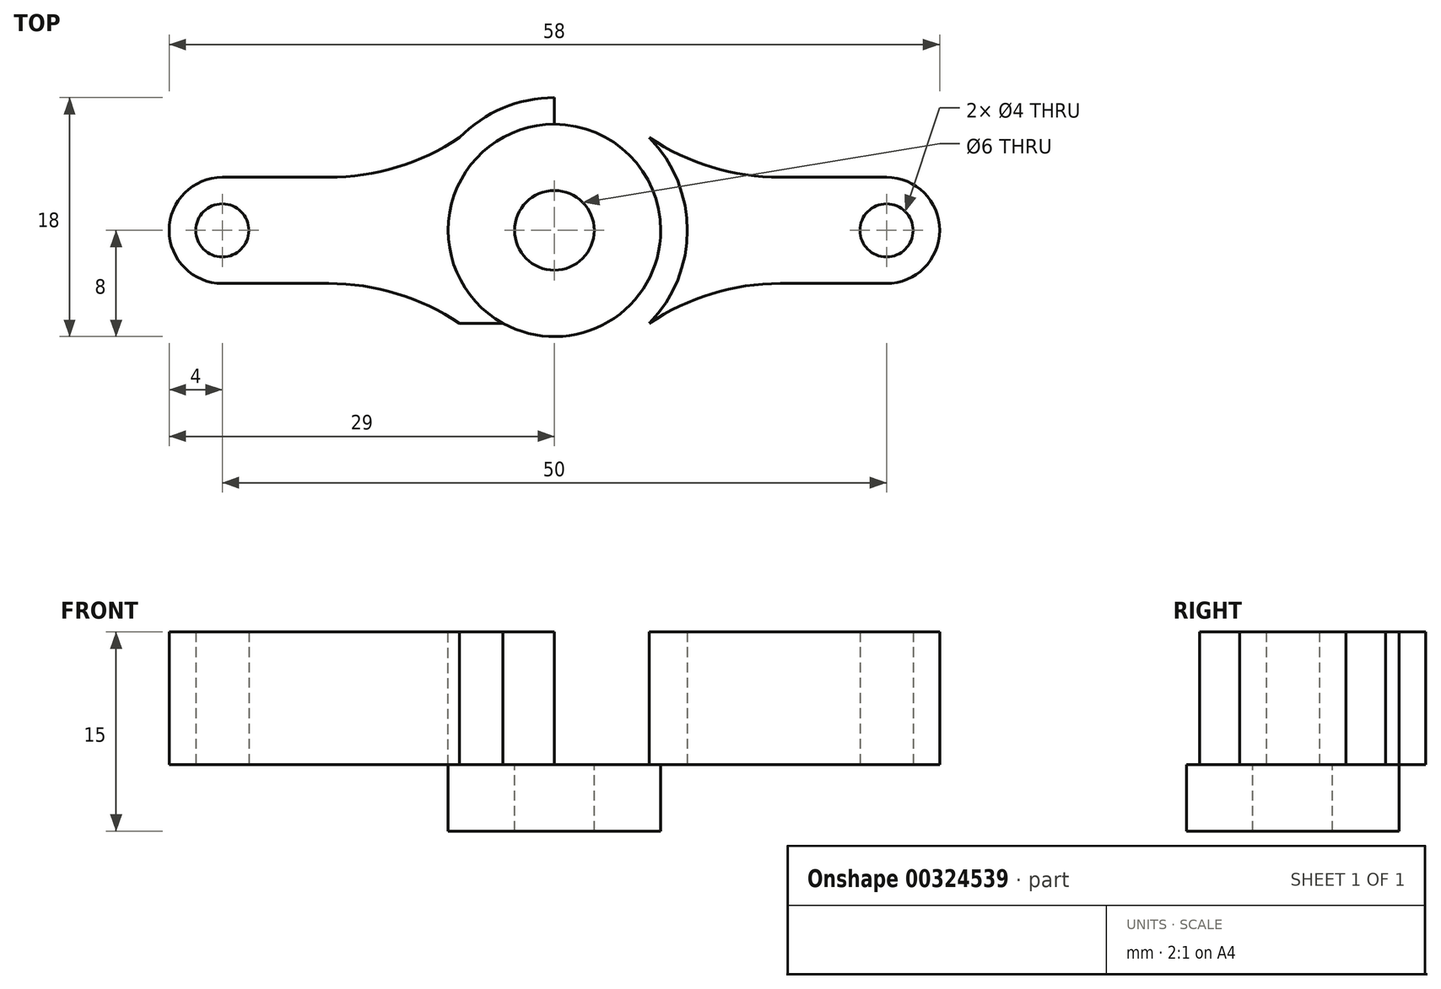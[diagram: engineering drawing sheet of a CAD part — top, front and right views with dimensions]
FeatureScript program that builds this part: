
annotation { "Feature Type Name" : "Feature", "Feature Type Description" : "" }
export const myFeature = defineFeature(function(context is Context, id is Id, definition is map)
    precondition{}
    {
        {
            var Q0;
            Q0=qCreatedBy(makeId("Top.planeOp"),FACE);
            var sketch = newSketch(context, id + "F0", { "sketchPlane" : qUnion([Q0])});
            skCircle(sketch, "E0", {"center": v(0, 0) * mm, "radius": 10 * mm});
            skCircle(sketch, "E1", {"center": v(25, 0) * mm, "radius": 4 * mm});
            skCircle(sketch, "E2", {"center": v(-25, 0) * mm, "radius": 4 * mm});
            skLineSegment(sketch, "E3", {"start": v(-25, 0) * mm, "end": v(-25, 4) * mm});
            skLineSegment(sketch, "E4", {"start": v(25, 0) * mm, "end": v(25, 4) * mm});
            skLineSegment(sketch, "E5", {"start": v(25, 0) * mm, "end": v(25, -4) * mm});
            skLineSegment(sketch, "E6", {"start": v(-25, 0) * mm, "end": v(-25, -4) * mm});
            skLineSegment(sketch, "E7", {"start": v(0, 0) * mm, "end": v(0, 10) * mm});
            skLineSegment(sketch, "E8", {"start": v(0, 10) * mm, "end": v(0, -10) * mm});
            skLineSegment(sketch, "E9", {"start": v(0, 7) * mm, "end": v(0, 10) * mm});
            skLineSegment(sketch, "E10", {"start": v(0, 7) * mm, "end": v(7.14, 7) * mm});
            skLineSegment(sketch, "E11", {"start": v(7.14, 7) * mm, "end": v(-7.14, 7) * mm});
            skLineSegment(sketch, "E12", {"start": v(25, 4) * mm, "end": v(17, 4) * mm});
            skArc(sketch, "E13", {"start": v(17, 4) * mm, "mid": v(11.85, 4.77) * mm, "end": v(7.14, 7) * mm});
            skLineSegment(sketch, "E14", {"start": v(0, -10) * mm, "end": v(0, -7) * mm});
            skLineSegment(sketch, "E15", {"start": v(0, -7) * mm, "end": v(7.14, -7) * mm});
            skLineSegment(sketch, "E16", {"start": v(7.14, -7) * mm, "end": v(-7.14, -7) * mm});
            skLineSegment(sketch, "E17", {"start": v(25, -4) * mm, "end": v(17, -4) * mm});
            skArc(sketch, "E18", {"start": v(17, -4) * mm, "mid": v(11.85, -4.77) * mm, "end": v(7.14, -7) * mm});
            skLineSegment(sketch, "E19", {"start": v(-25, 4) * mm, "end": v(-17, 4) * mm});
            skLineSegment(sketch, "E20", {"start": v(-25, -4) * mm, "end": v(-17, -4) * mm});
            skArc(sketch, "E21", {"start": v(-17, 4) * mm, "mid": v(-11.85, 4.77) * mm, "end": v(-7.14, 7) * mm});
            skArc(sketch, "E22", {"start": v(-17, -4) * mm, "mid": v(-11.85, -4.77) * mm, "end": v(-7.14, -7) * mm});
            skCircle(sketch, "E23", {"center": v(0, 0) * mm, "radius": 7.5 * mm});
            skCircle(sketch, "E24", {"center": v(0, 0) * mm, "radius": 3 * mm});
            skCircle(sketch, "E25", {"center": v(-25, 0) * mm, "radius": 2 * mm});
            skCircle(sketch, "E26", {"center": v(25, 0) * mm, "radius": 2 * mm});
            skSolve(sketch);
        }
        {
            var Q0;
            {var subQ0=sQuery(id+"F0.wireOp",EDGE,"E3");var subQ5=sQuery(id+"F0.wireOp",EDGE,"E25");var subQ6=makeQuery(id+"F0.imprint","INTERSECT",VERTEX,{"derivedFrom":[subQ0,subQ5]});Q0=makeQuery(id+"F0.imprint","IMPRINT",FACE,{"disambiguationData":[TD([[makeQuery(id+"F0.imprint","IMPRINT",EDGE,{"disambiguationData":[TD([[subQ6,-1.0]])],"derivedFrom":subQ5}),-1.0]])]});}
            var Q1;
            {var subQ0=sQuery(id+"F0.wireOp",EDGE,"E3");var subQ5=sQuery(id+"F0.wireOp",EDGE,"E25");var subQ6=makeQuery(id+"F0.imprint","INTERSECT",VERTEX,{"derivedFrom":[subQ0,subQ5]});Q1=makeQuery(id+"F0.imprint","IMPRINT",FACE,{"disambiguationData":[TD([[makeQuery(id+"F0.imprint","IMPRINT",EDGE,{"disambiguationData":[TD([[subQ6,1.0]])],"derivedFrom":subQ5}),-1.0]])]});}
            var Q2;
            {var subQ0=sQuery(id+"F0.wireOp",EDGE,"E19");Q2=makeQuery(id+"F0.imprint","IMPRINT",FACE,{"disambiguationData":[TD([[makeQuery(id+"F0.imprint","IMPRINT",EDGE,{"derivedFrom":subQ0}),-1.0]])]});}
            var Q3;
            {var subQ0=sQuery(id+"F0.wireOp",EDGE,"E11");var subQ5=sQuery(id+"F0.wireOp",EDGE,"E23");var subQ6=makeQuery(id+"F0.imprint","INTERSECT",VERTEX,{"disambiguationData":[OD(1.0)],"derivedFrom":[subQ0,subQ5]});Q3=makeQuery(id+"F0.imprint","IMPRINT",FACE,{"disambiguationData":[TD([[makeQuery(id+"F0.imprint","IMPRINT",EDGE,{"disambiguationData":[TD([[subQ6,-1.0]])],"derivedFrom":subQ5}),-1.0]])]});}
            var Q4;
            {var subQ0=sQuery(id+"F0.wireOp",EDGE,"E11");var subQ5=sQuery(id+"F0.wireOp",EDGE,"E23");var subQ6=makeQuery(id+"F0.imprint","INTERSECT",VERTEX,{"disambiguationData":[OD(0.0)],"derivedFrom":[subQ0,subQ5]});Q4=makeQuery(id+"F0.imprint","IMPRINT",FACE,{"disambiguationData":[TD([[makeQuery(id+"F0.imprint","IMPRINT",EDGE,{"disambiguationData":[TD([[subQ6,1.0]])],"derivedFrom":subQ5}),-1.0]])]});}
            var Q5;
            {var subQ0=sQuery(id+"F0.wireOp",EDGE,"E8");var subQ1=makeQuery(id+"F0.imprint","IMPRINT",VERTEX,{"derivedFrom":subQ0});Q5=makeQuery(id+"F0.imprint","IMPRINT",FACE,{"disambiguationData":[TD([[makeQuery(id+"F0.imprint","IMPRINT",EDGE,{"disambiguationData":[TD([[subQ1,1.0]])],"derivedFrom":subQ0}),1.0]])]});}
            var Q6;
            {var subQ0=sQuery(id+"F0.wireOp",EDGE,"E8");var subQ1=makeQuery(id+"F0.imprint","IMPRINT",VERTEX,{"derivedFrom":subQ0});Q6=makeQuery(id+"F0.imprint","IMPRINT",FACE,{"disambiguationData":[TD([[makeQuery(id+"F0.imprint","IMPRINT",EDGE,{"disambiguationData":[TD([[subQ1,1.0]])],"derivedFrom":subQ0}),-1.0]])]});}
            var Q7;
            {var subQ1=sQuery(id+"F0.wireOp",EDGE,"E12");Q7=makeQuery(id+"F0.imprint","IMPRINT",FACE,{"disambiguationData":[TD([[makeQuery(id+"F0.imprint","IMPRINT",EDGE,{"derivedFrom":subQ1}),1.0]])]});}
            var Q8;
            {var subQ1=sQuery(id+"F0.wireOp",EDGE,"E14");var subQ3=sQuery(id+"F0.wireOp",EDGE,"E23");var subQ4=makeQuery(id+"F0.imprint","INTERSECT",VERTEX,{"derivedFrom":[subQ1,subQ3]});Q8=makeQuery(id+"F0.imprint","IMPRINT",FACE,{"disambiguationData":[TD([[makeQuery(id+"F0.imprint","IMPRINT",EDGE,{"disambiguationData":[TD([[subQ4,1.0]])],"derivedFrom":subQ3}),1.0]])]});}
            var Q9;
            {var subQ1=sQuery(id+"F0.wireOp",EDGE,"E14");var subQ3=sQuery(id+"F0.wireOp",EDGE,"E23");var subQ4=makeQuery(id+"F0.imprint","INTERSECT",VERTEX,{"derivedFrom":[subQ1,subQ3]});Q9=makeQuery(id+"F0.imprint","IMPRINT",FACE,{"disambiguationData":[TD([[makeQuery(id+"F0.imprint","IMPRINT",EDGE,{"disambiguationData":[TD([[subQ4,-1.0]])],"derivedFrom":subQ3}),1.0]])]});}
            var Q10;
            {var subQ0=sQuery(id+"F0.wireOp",EDGE,"E14");var subQ1=sQuery(id+"F0.wireOp",EDGE,"E0");var subQ2=makeQuery(id+"F0.imprint","INTERSECT",VERTEX,{"derivedFrom":[subQ1,subQ0]});Q10=makeQuery(id+"F0.imprint","IMPRINT",FACE,{"disambiguationData":[TD([[makeQuery(id+"F0.imprint","IMPRINT",EDGE,{"disambiguationData":[TD([[subQ2,-1.0]])],"derivedFrom":subQ0}),-1.0]])]});}
            var Q11;
            {var subQ0=sQuery(id+"F0.wireOp",EDGE,"E14");var subQ1=sQuery(id+"F0.wireOp",EDGE,"E0");var subQ2=makeQuery(id+"F0.imprint","INTERSECT",VERTEX,{"derivedFrom":[subQ1,subQ0]});Q11=makeQuery(id+"F0.imprint","IMPRINT",FACE,{"disambiguationData":[TD([[makeQuery(id+"F0.imprint","IMPRINT",EDGE,{"disambiguationData":[TD([[subQ2,-1.0]])],"derivedFrom":subQ0}),1.0]])]});}
            var Q12;
            {var subQ3=sQuery(id+"F0.wireOp",EDGE,"E23");var subQ5=sQuery(id+"F0.wireOp",EDGE,"E11");var subQ7=makeQuery(id+"F0.imprint","INTERSECT",VERTEX,{"disambiguationData":[OD(1.0)],"derivedFrom":[subQ5,subQ3]});Q12=makeQuery(id+"F0.imprint","IMPRINT",FACE,{"disambiguationData":[TD([[makeQuery(id+"F0.imprint","IMPRINT",EDGE,{"disambiguationData":[TD([[subQ7,-1.0]])],"derivedFrom":subQ3}),1.0]])]});}
            var Q13;
            {var subQ0=sQuery(id+"F0.wireOp",EDGE,"E11");var subQ3=sQuery(id+"F0.wireOp",EDGE,"E23");var subQ4=makeQuery(id+"F0.imprint","INTERSECT",VERTEX,{"disambiguationData":[OD(0.0)],"derivedFrom":[subQ0,subQ3]});Q13=makeQuery(id+"F0.imprint","IMPRINT",FACE,{"disambiguationData":[TD([[makeQuery(id+"F0.imprint","IMPRINT",EDGE,{"disambiguationData":[TD([[subQ4,1.0]])],"derivedFrom":subQ3}),1.0]])]});}
            var Q14;
            {var subQ0=sQuery(id+"F0.wireOp",EDGE,"E4");var subQ5=sQuery(id+"F0.wireOp",EDGE,"E26");var subQ6=makeQuery(id+"F0.imprint","INTERSECT",VERTEX,{"derivedFrom":[subQ0,subQ5]});Q14=makeQuery(id+"F0.imprint","IMPRINT",FACE,{"disambiguationData":[TD([[makeQuery(id+"F0.imprint","IMPRINT",EDGE,{"disambiguationData":[TD([[subQ6,-1.0]])],"derivedFrom":subQ5}),-1.0]])]});}
            var Q15;
            {var subQ0=sQuery(id+"F0.wireOp",EDGE,"E4");var subQ5=sQuery(id+"F0.wireOp",EDGE,"E26");var subQ6=makeQuery(id+"F0.imprint","INTERSECT",VERTEX,{"derivedFrom":[subQ0,subQ5]});Q15=makeQuery(id+"F0.imprint","IMPRINT",FACE,{"disambiguationData":[TD([[makeQuery(id+"F0.imprint","IMPRINT",EDGE,{"disambiguationData":[TD([[subQ6,1.0]])],"derivedFrom":subQ5}),-1.0]])]});}
            var Q16;
            {var subQ1=sQuery(id+"F0.wireOp",EDGE,"E9");var subQ3=sQuery(id+"F0.wireOp",EDGE,"E23");var subQ4=makeQuery(id+"F0.imprint","INTERSECT",VERTEX,{"derivedFrom":[subQ1,subQ3]});Q16=makeQuery(id+"F0.imprint","IMPRINT",FACE,{"disambiguationData":[TD([[makeQuery(id+"F0.imprint","IMPRINT",EDGE,{"disambiguationData":[TD([[subQ4,-1.0]])],"derivedFrom":subQ3}),1.0]])]});}
            var Q17;
            {var subQ1=sQuery(id+"F0.wireOp",EDGE,"E9");var subQ3=sQuery(id+"F0.wireOp",EDGE,"E23");var subQ4=makeQuery(id+"F0.imprint","INTERSECT",VERTEX,{"derivedFrom":[subQ1,subQ3]});Q17=makeQuery(id+"F0.imprint","IMPRINT",FACE,{"disambiguationData":[TD([[makeQuery(id+"F0.imprint","IMPRINT",EDGE,{"disambiguationData":[TD([[subQ4,1.0]])],"derivedFrom":subQ3}),1.0]])]});}
            var Q18;
            {var subQ0=sQuery(id+"F0.wireOp",EDGE,"E9");var subQ1=sQuery(id+"F0.wireOp",EDGE,"E0");var subQ2=makeQuery(id+"F0.imprint","INTERSECT",VERTEX,{"derivedFrom":[subQ1,subQ0]});Q18=makeQuery(id+"F0.imprint","IMPRINT",FACE,{"disambiguationData":[TD([[makeQuery(id+"F0.imprint","IMPRINT",EDGE,{"disambiguationData":[TD([[subQ2,1.0]])],"derivedFrom":subQ0}),1.0]])]});}
            var Q19;
            {var subQ0=sQuery(id+"F0.wireOp",EDGE,"E9");var subQ1=sQuery(id+"F0.wireOp",EDGE,"E0");var subQ2=makeQuery(id+"F0.imprint","INTERSECT",VERTEX,{"derivedFrom":[subQ1,subQ0]});Q19=makeQuery(id+"F0.imprint","IMPRINT",FACE,{"disambiguationData":[TD([[makeQuery(id+"F0.imprint","IMPRINT",EDGE,{"disambiguationData":[TD([[subQ2,1.0]])],"derivedFrom":subQ0}),-1.0]])]});}
            extrude(context, id + "F1", {"entities" : qUnion([Q0, Q1, Q2, Q3, Q4, Q5, Q6, Q7, Q8, Q9, Q10, Q11, Q12, Q13, Q14, Q15, Q16, Q17, Q18, Q19]), "depth" : 10 * mm});
        }
        {
            var Q0;
            Q0=makeQuery(id+"F1.opExtrude","CAP_FACE",FACE,{"disambiguationData":[OSD([sQuery(id+"F0.wireOp",EDGE,"E0"),sQuery(id+"F0.wireOp",EDGE,"E1"),sQuery(id+"F0.wireOp",EDGE,"E2"),sQuery(id+"F0.wireOp",EDGE,"E12"),sQuery(id+"F0.wireOp",EDGE,"E13"),sQuery(id+"F0.wireOp",EDGE,"E17"),sQuery(id+"F0.wireOp",EDGE,"E18"),sQuery(id+"F0.wireOp",EDGE,"E19"),sQuery(id+"F0.wireOp",EDGE,"E20"),sQuery(id+"F0.wireOp",EDGE,"E21"),sQuery(id+"F0.wireOp",EDGE,"E22"),sQuery(id+"F0.wireOp",EDGE,"E25"),sQuery(id+"F0.wireOp",EDGE,"E26")])],"isStart":false});
            var sketch = newSketch(context, id + "F2", { "sketchPlane" : qUnion([Q0])});
            skCircle(sketch, "E27", {"center": v(0, 0) * mm, "radius": 8 * mm});
            skSolve(sketch);
        }
        {
            var Q0;
            Q0 = qSketchRegion(id + "F2", true);
            extrude(context, id + "F3", {"entities" : qUnion([Q0]), "operationType" : NewBodyOperationType.ADD, "oppositeDirection" : true, "depth" : 15 * mm});
        }
        {
            var Q0;
            Q0=makeQuery(id+"F1.opExtrude","CAP_FACE",FACE,{"disambiguationData":[OSD([sQuery(id+"F0.wireOp",EDGE,"E0"),sQuery(id+"F0.wireOp",EDGE,"E1"),sQuery(id+"F0.wireOp",EDGE,"E2"),sQuery(id+"F0.wireOp",EDGE,"E12"),sQuery(id+"F0.wireOp",EDGE,"E13"),sQuery(id+"F0.wireOp",EDGE,"E17"),sQuery(id+"F0.wireOp",EDGE,"E18"),sQuery(id+"F0.wireOp",EDGE,"E19"),sQuery(id+"F0.wireOp",EDGE,"E20"),sQuery(id+"F0.wireOp",EDGE,"E21"),sQuery(id+"F0.wireOp",EDGE,"E22"),sQuery(id+"F0.wireOp",EDGE,"E25"),sQuery(id+"F0.wireOp",EDGE,"E26")])],"isStart":false});
            var sketch = newSketch(context, id + "F4", { "sketchPlane" : qUnion([Q0])});
            skCircle(sketch, "E28", {"center": v(0, 0) * mm, "radius": 8 * mm});
            skSolve(sketch);
        }
        {
            var Q0;
            Q0 = qSketchRegion(id + "F4", true);
            extrude(context, id + "F5", {"entities" : qUnion([Q0]), "operationType" : NewBodyOperationType.REMOVE, "oppositeDirection" : true, "depth" : 10 * mm});
        }
        {
            var Q0;
            Q0=qCreatedBy(makeId("Top.planeOp"),FACE);
            var sketch = newSketch(context, id + "F6", { "sketchPlane" : qUnion([Q0])});
            skCircle(sketch, "E29", {"center": v(0, 0) * mm, "radius": 3 * mm});
            skSolve(sketch);
        }
        {
            var Q0;
            Q0 = qSketchRegion(id + "F6", true);
            extrude(context, id + "F7", {"entities" : qUnion([Q0]), "operationType" : NewBodyOperationType.REMOVE, "oppositeDirection" : true, "depth" : 25 * mm});
        }
    });
